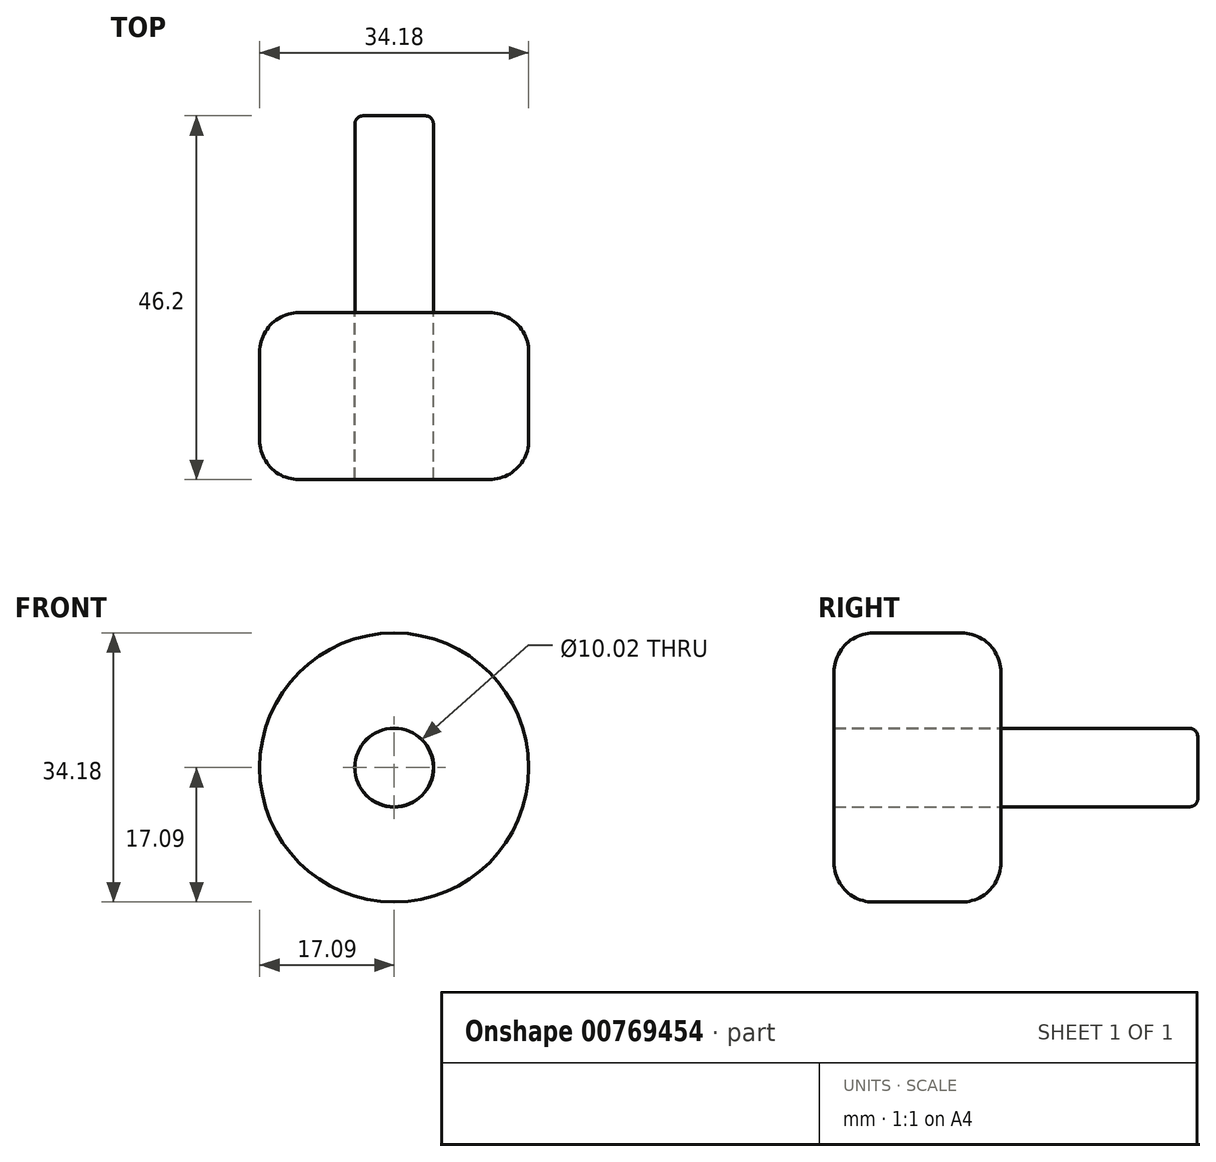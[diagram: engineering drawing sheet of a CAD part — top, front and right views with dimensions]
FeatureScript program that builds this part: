
annotation { "Feature Type Name" : "Feature", "Feature Type Description" : "" }
export const myFeature = defineFeature(function(context is Context, id is Id, definition is map)
    precondition{}
    {
        {
            var Q0;
            Q0=qCreatedBy(makeId("Front.planeOp"),FACE);
            var sketch = newSketch(context, id + "F0", { "sketchPlane" : qUnion([Q0])});
            skCircle(sketch, "E0", {"center": v(0, 0) * mm, "radius": 4.97 * mm});
            skSolve(sketch);
        }
        {
            var Q0;
            Q0 = qSketchRegion(id + "F0", true);
            extrude(context, id + "F1", {"entities" : qUnion([Q0]), "depth" : 25 * mm, "offsetDistance" : 25 * mm});
        }
        {
            var Q0;
            Q0=makeQuery(id+"F1.opExtrude","CAP_FACE",FACE,{"disambiguationData":[OSD([sQuery(id+"F0.wireOp",EDGE,"E0")])],"isStart":false});
            var sketch = newSketch(context, id + "F2", { "sketchPlane" : qUnion([Q0])});
            skCircle(sketch, "E1", {"center": v(0, 0) * mm, "radius": 5 * mm});
            skCircle(sketch, "E2", {"center": v(0, 0) * mm, "radius": 17.1 * mm});
            skSolve(sketch);
        }
        {
            var Q0;
            Q0 = qSketchRegion(id + "F2", true);
            var Q1;
            Q1=makeQuery(id+"F2.imprint","IMPRINT",FACE,{"disambiguationData":[TD([[makeQuery(id+"F2.imprint","IMPRINT",EDGE,{"derivedFrom":makeQuery(id+"F1.opExtrude","CAP_EDGE",EDGE,{"disambiguationData":[OSD([sQuery(id+"F0.wireOp",EDGE,"E0")])],"isStart":false})}),1.0]])]});
            extrude(context, id + "F3", {"entities" : qUnion([Q0, Q1]), "operationType" : NewBodyOperationType.ADD, "depth" : 21.2 * mm, "offsetDistance" : 25 * mm});
        }
        {
            var Q0;
            Q0=makeQuery(id+"F3.opExtrude","CAP_EDGE",EDGE,{"disambiguationData":[OSD([sQuery(id+"F2.wireOp",EDGE,"E2")])],"isStart":false});
            fillet(context, id + "F4", {"entities" : qUnion([Q0]), "radius" : 5 * mm, "tangentPropagation" : true, "allowEdgeOverflow" : false});
        }
        {
            var Q0;
            Q0=makeQuery(id+"F3.opExtrude","CAP_EDGE",EDGE,{"disambiguationData":[OSD([sQuery(id+"F2.wireOp",EDGE,"E2")])],"isStart":true});
            fillet(context, id + "F5", {"entities" : qUnion([Q0]), "radius" : 5 * mm, "tangentPropagation" : true, "allowEdgeOverflow" : false});
        }
        {
            var Q0;
            Q0=makeQuery(id+"F1.opExtrude","CAP_EDGE",EDGE,{"disambiguationData":[OSD([sQuery(id+"F0.wireOp",EDGE,"E0")])],"isStart":true});
            fillet(context, id + "F6", {"entities" : qUnion([Q0]), "radius" : 1 * mm, "tangentPropagation" : true, "allowEdgeOverflow" : false});
        }
    });
